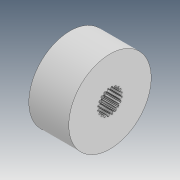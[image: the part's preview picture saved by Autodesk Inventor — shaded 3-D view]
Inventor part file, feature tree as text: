
AUTODESK INVENTOR PART (.ipt)
format: ipt  version: 2021 (Build 250183000, 183)  size: 293,376 bytes
history: native  units: in
note: dims shown in document units (in); Inventor stores cm internally (conversion verified against a paired STEP export)
features: extrude x3, sketch x3, other x2
ambient origin geometry x8: Origin, YZ Plane, XZ Plane, XY Plane, X Axis, Y Axis, Z Axis, Center Point
bodies: Body1 (feature_tree)
feature tree (8):
  other  "Sólido1"
  other  "Revolução1"
  extrude  "Extrusão1"  Depth=0.3858in
  extrude  "Extrusão2"  Depth=0.1378in
  extrude  "Extrusão5"  Depth=0.1378in
  sketch  "Esboço2"  dims[d0=0.374in d1=0.3858in]
  sketch  "Esboço3"  dims[d2=90.0deg d3=0.1378in]
  sketch  "Esboço4"  dims[d4=0.1909in d5=0.0in d6=0.3543in d7=0.0787in d8=0.0in d58=0.2008in d59=0.2323in d60=0.0024in d61=0.0024in d62=0.002in d63=0.002in d64=7.874in d66=360.0deg d68=0.1378in d69=0.0in]
